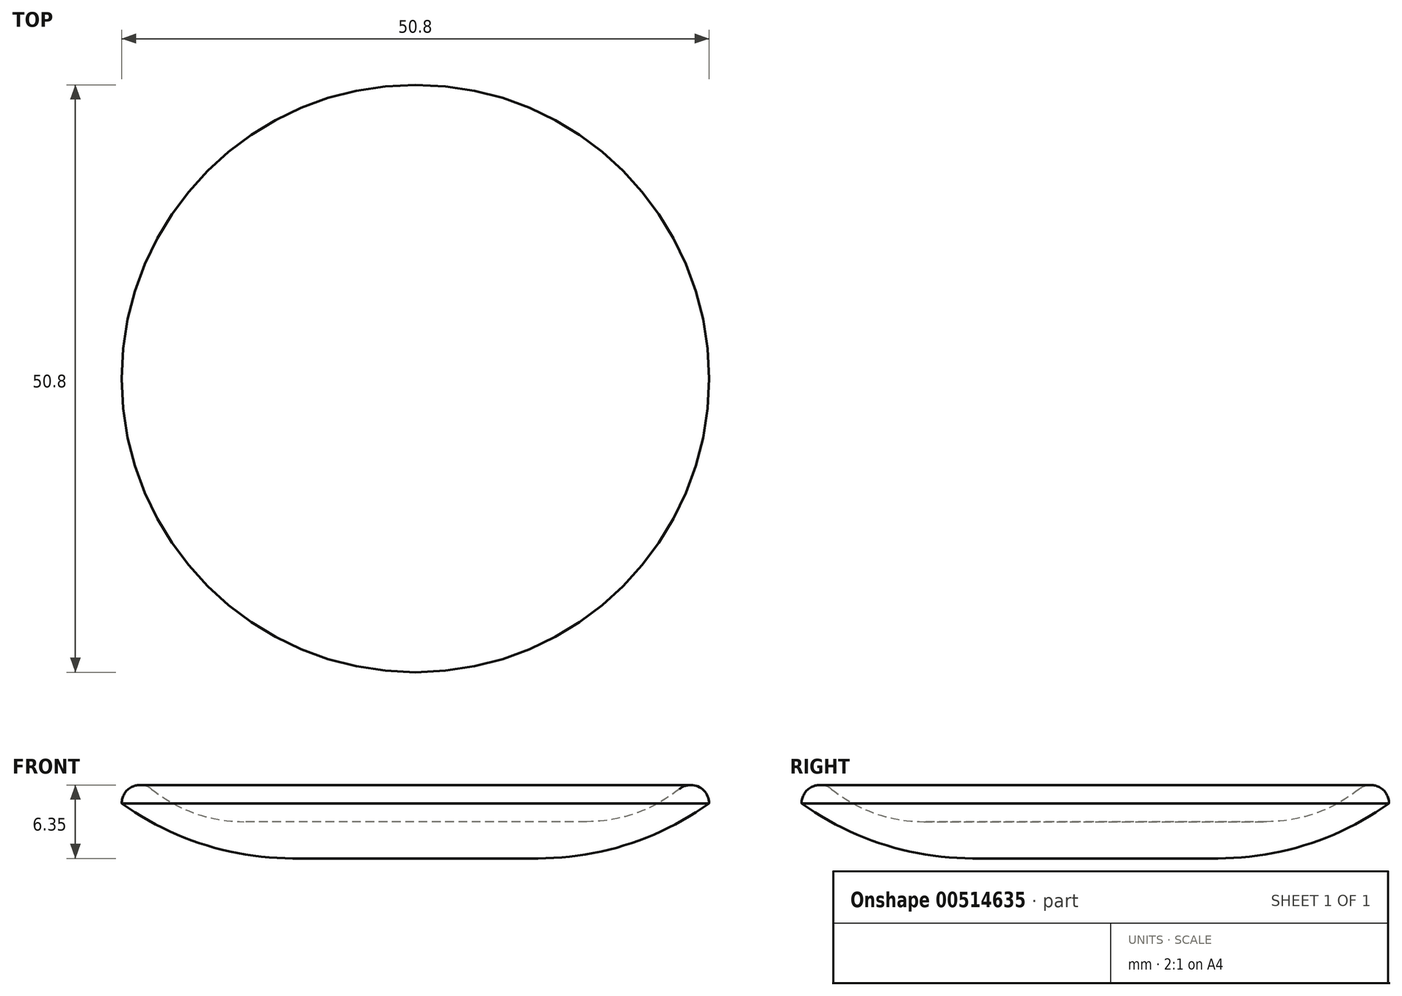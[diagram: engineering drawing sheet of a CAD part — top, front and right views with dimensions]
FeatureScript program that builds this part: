
annotation { "Feature Type Name" : "Feature", "Feature Type Description" : "" }
export const myFeature = defineFeature(function(context is Context, id is Id, definition is map)
    precondition{}
    {
        {
            var Q0;
            Q0=qCreatedBy(makeId("Top.planeOp"),FACE);
            var sketch = newSketch(context, id + "F0", { "sketchPlane" : qUnion([Q0])});
            skCircle(sketch, "E0", {"center": v(0, 0) * mm, "radius": 25.4 * mm});
            skCircle(sketch, "E1.0", {"center": v(0, 0) * mm, "radius": 22.23 * mm});
            skSolve(sketch);
        }
        {
            var Q0;
            Q0=makeQuery(id+"F0.imprint","IMPRINT",FACE,{"disambiguationData":[TD([[makeQuery(id+"F0.imprint","IMPRINT",EDGE,{"derivedFrom":sQuery(id+"F0.wireOp",EDGE,"E0")}),1.0]])]});
            extrude(context, id + "F1", {"entities" : qUnion([Q0]), "depth" : 6.35 * mm, "offsetDistance" : 25.4 * mm});
        }
        {
            var Q0;
            Q0=makeQuery(id+"F0.imprint","IMPRINT",FACE,{"disambiguationData":[TD([[makeQuery(id+"F0.imprint","IMPRINT",EDGE,{"derivedFrom":sQuery(id+"F0.wireOp",EDGE,"E1.0")}),1.0]])]});
            extrude(context, id + "F2", {"entities" : qUnion([Q0]), "operationType" : NewBodyOperationType.ADD, "depth" : 3.17 * mm, "offsetDistance" : 25.4 * mm});
        }
        {
            var Q0;
            Q0=makeQuery(id+"F1.opExtrude","CAP_EDGE",EDGE,{"disambiguationData":[OSD([sQuery(id+"F0.wireOp",EDGE,"E1.0")])],"isStart":false});
            fillet(context, id + "F3", {"entities" : qUnion([Q0]), "radius" : 1.59 * mm, "tangentPropagation" : true, "allowEdgeOverflow" : false});
        }
        {
            var Q0;
            Q0=makeQuery(id+"F1.opExtrude","CAP_EDGE",EDGE,{"disambiguationData":[OSD([sQuery(id+"F0.wireOp",EDGE,"E0")])],"isStart":false});
            fillet(context, id + "F4", {"entities" : qUnion([Q0]), "radius" : 1.59 * mm, "tangentPropagation" : true, "allowEdgeOverflow" : false});
        }
        {
            var Q0;
            Q0=makeQuery(id+"F2.opExtrude","CAP_FACE",FACE,{"disambiguationData":[OSD([sQuery(id+"F0.wireOp",EDGE,"E1.0")])],"isStart":false});
            fillet(context, id + "F5", {"entities" : qUnion([Q0]), "radius" : 12.7 * mm, "tangentPropagation" : true, "allowEdgeOverflow" : false});
        }
        {
            var Q0;
            Q0=makeQuery(id+"F1.opExtrude","CAP_EDGE",EDGE,{"disambiguationData":[OSD([sQuery(id+"F0.wireOp",EDGE,"E0")])],"isStart":true});
            fillet(context, id + "F6", {"entities" : qUnion([Q0]), "radius" : 25.4 * mm, "tangentPropagation" : true, "allowEdgeOverflow" : false});
        }
    });
